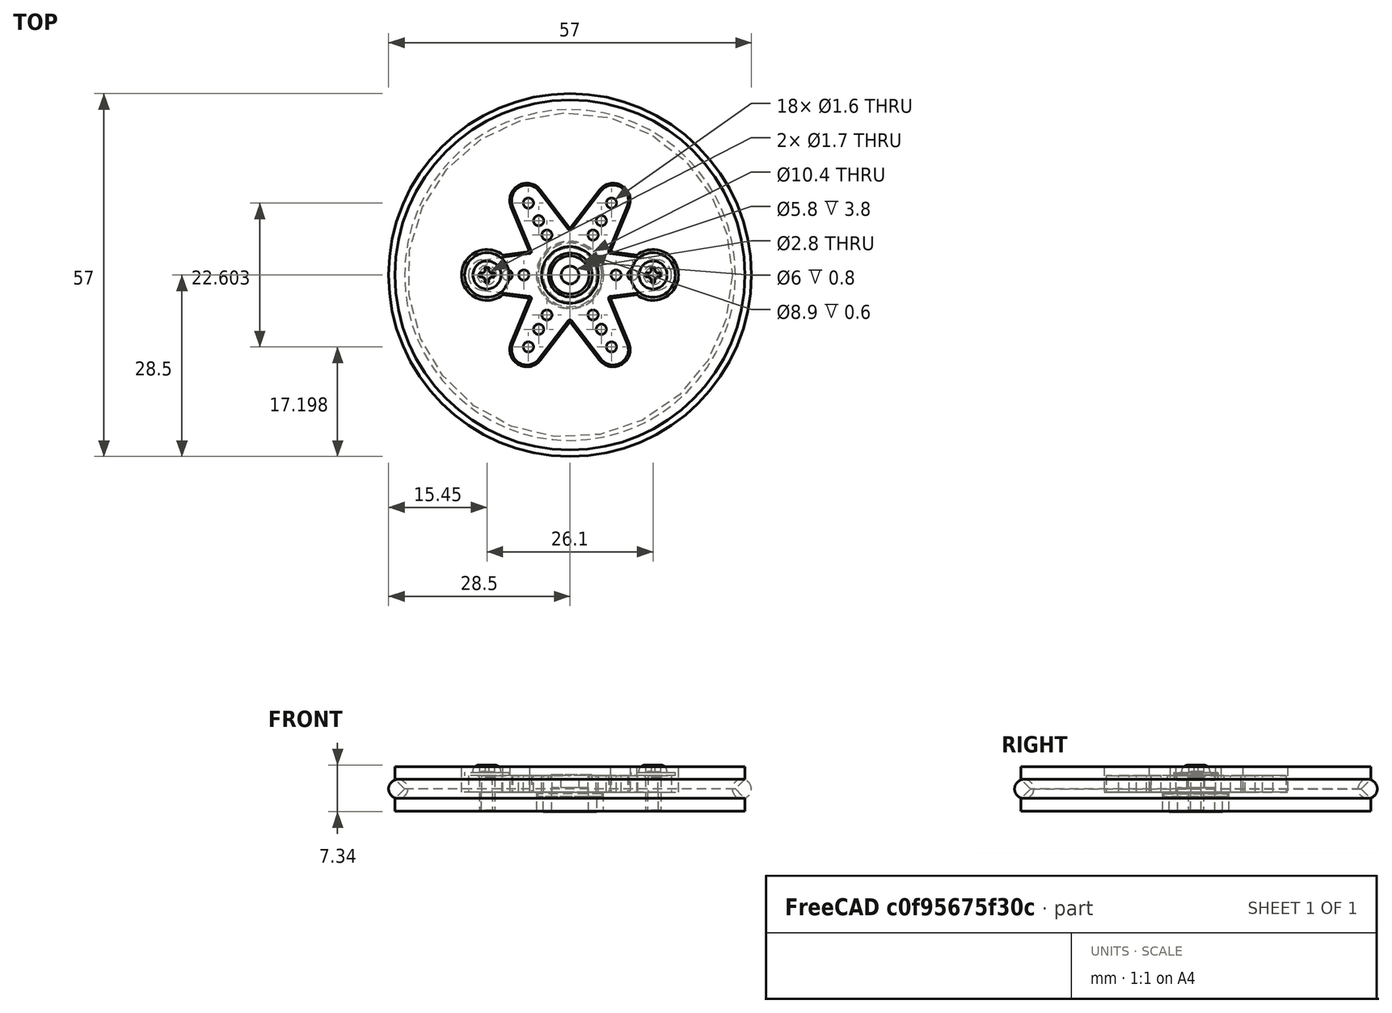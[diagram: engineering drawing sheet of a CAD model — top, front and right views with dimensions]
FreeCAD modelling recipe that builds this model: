
FCSTD DOCUMENT  (FreeCAD 0.14R3702 (Git))
Label: Renacuajo-wheel-6-arms-horn-assembly
License: CC-BY 3.0
LicenseURL: http://creativecommons.org/licenses/by/3.0/
objects: Part::Feature×4, Part::Torus×1, Part::Compound×1
note: 6 computed .brp shape members not serialized (recipe doc carries the construction recipe); baked Part::Feature solids carry a one-line shape summary decoded from their .brp

FEATURE [Part::Feature] PolarPattern  label="Renacuajo-wheel-6-arms-horn"
  shape: bbox 55 x 55 x 7.002 mm, 34 faces (baked)
FEATURE [Part::Feature] Fillet  label="Horn-6-arms-final001"
  Placement = pos=(0,0,-0.49) rot=(0,0,1;0rad)
  shape: bbox 31.9 x 28.27 x 5.8 mm, 60 faces (baked)
FEATURE [Part::Feature] Chamfer  label="screw002"
  Placement = pos=(-13.05,0,2.11) rot=(0,0,1;0rad)
  shape: bbox 7 x 7 x 7.14 mm, 33 faces (baked)
FEATURE [Part::Feature] Chamfer001  label="screw1"
  Placement = pos=(13.05,0,2.11) rot=(0,0,1;0rad)
  shape: bbox 7 x 7 x 7.14 mm, 33 faces (baked)
FEATURE [Part::Torus] Torus  label="o-ring"
  Angle1 = -180
  Angle2 = 180
  Angle3 = 360
  Radius1 = 27
  Radius2 = 1.5
FEATURE [Part::Compound] Compound  label="Renacuajo-wheel-6-arms-horn-assembly"
  Links = -> [PolarPattern,Fillet,Chamfer,Torus,Chamfer001]
